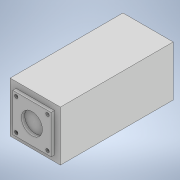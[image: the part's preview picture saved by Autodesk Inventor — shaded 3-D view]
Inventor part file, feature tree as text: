
AUTODESK INVENTOR PART (.ipt)
format: ipt  version: 2022.2 (Build 262287030, 287C)  size: 125,440 bytes
history: native  units: in
note: dims shown in document units (in); Inventor stores cm internally (conversion verified against a paired STEP export)
features: sketch x3, extrude x2, projected_geometry x2, hole x1
ambient origin geometry x8: Origin, YZ Plane, XZ Plane, XY Plane, X Axis, Y Axis, Z Axis, Center Point
bodies: Solid1 (feature_tree)
feature tree (8):
  extrude  "Extrusion1"  Depth=0.8858in
  extrude  "Extrusion4"  Depth=0.6772in
  hole  "Hole3"  [1 undecoded]
  sketch  "Sketch1"  dims[d0=0.8858in d1=0.8858in]
  sketch  "Sketch8"  dims[d2=1.9882in d3=0.0in d41=0.6772in]
  sketch  "Sketch9"  dims[d42=0.6772in d43=0.3713in d44=0.0591in d45=0.0in d46=0.7874in d48=0.5512in d49=0.7874in d51=0.5512in d54=0.2756in d55=0.2756in d56=0.0617in d57=0.0984in d58=0.1476in d59=0.0984in d60=90.0deg d61=0.1181in d62=0.8108in]
  projected_geometry  "Projected Loop1"
  projected_geometry  "Projected Loop2"
note: 1 required parameter value undecoded (feature->parameter linkage not recoverable at this tier; creation-order binding heuristic only, values carry confidence <= 0.55)
